# Revit family: RHA, RHG
name_source: partatom
category: Generic Models
revit_build: Autodesk Revit 2018 (Build: 20170223_1515(x64)
units: mm (PartAtom-declared; Revit-internal decimal feet)

## family parameters
Can host rebar = No
Cut with Voids When Loaded = No
Host = Face
Part Type = Normal
Room Calculation Point = No
Round Connector Dimension = Use Diameter
Shared = No

## types (10) — shared parameters
Default Elevation = 4' - 0"
Description = ROOF HATCH
Manufacturer = MIFAB
Material = <By Category>
Model = RHA, RHG
URL = WWW.MIFAB.COM

## per-type parameters (varying)
| type | Height | Width |
| RHA, RHG-24"x24" | 2' - 0" | 2' - 0" |
| RHA, RHG-24"x30" | 2' - 6" | 2' - 0" |
| RHA, RHG-24"x36" | 3' - 0" | 2' - 0" |
| RHA, RHG-30"x30" | 2' - 6" | 2' - 6" |
| RHA, RHG-30"x36" | 3' - 0" | 2' - 6" |
| RHA, RHG-30"x54" | 4' - 6" | 2' - 6" |
| RHA, RHG-30"x96" | 4' - 6" | 2' - 6" |
| RHA, RHG-36"x36" | 3' - 0" | 3' - 0" |
| RHA, RHG-36"x48" | 4' - 0" | 3' - 0" |
| RHA, RHG-48"x48" | 4' - 0" | 4' - 0" |

## geometry (parser evidence)
native form markers: Sweep x5
no freeform markers — native parametric forms only
